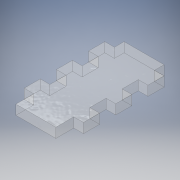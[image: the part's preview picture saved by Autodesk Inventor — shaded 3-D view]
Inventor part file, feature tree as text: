
AUTODESK INVENTOR PART (.ipt)
format: ipt  version: 2019 (Build 230136000, 136)  size: 143,872 bytes
history: native  units: mm
features: extrude x1
ambient origin geometry x8: Origin, YZ Plane, XZ Plane, XY Plane, X Axis, Y Axis, Z Axis, Center Point
bodies: Body1 (feature_tree)
feature tree (1):
  extrude  "Extrusion2"  Depth=6.0mm TaperAngle=0.0deg
